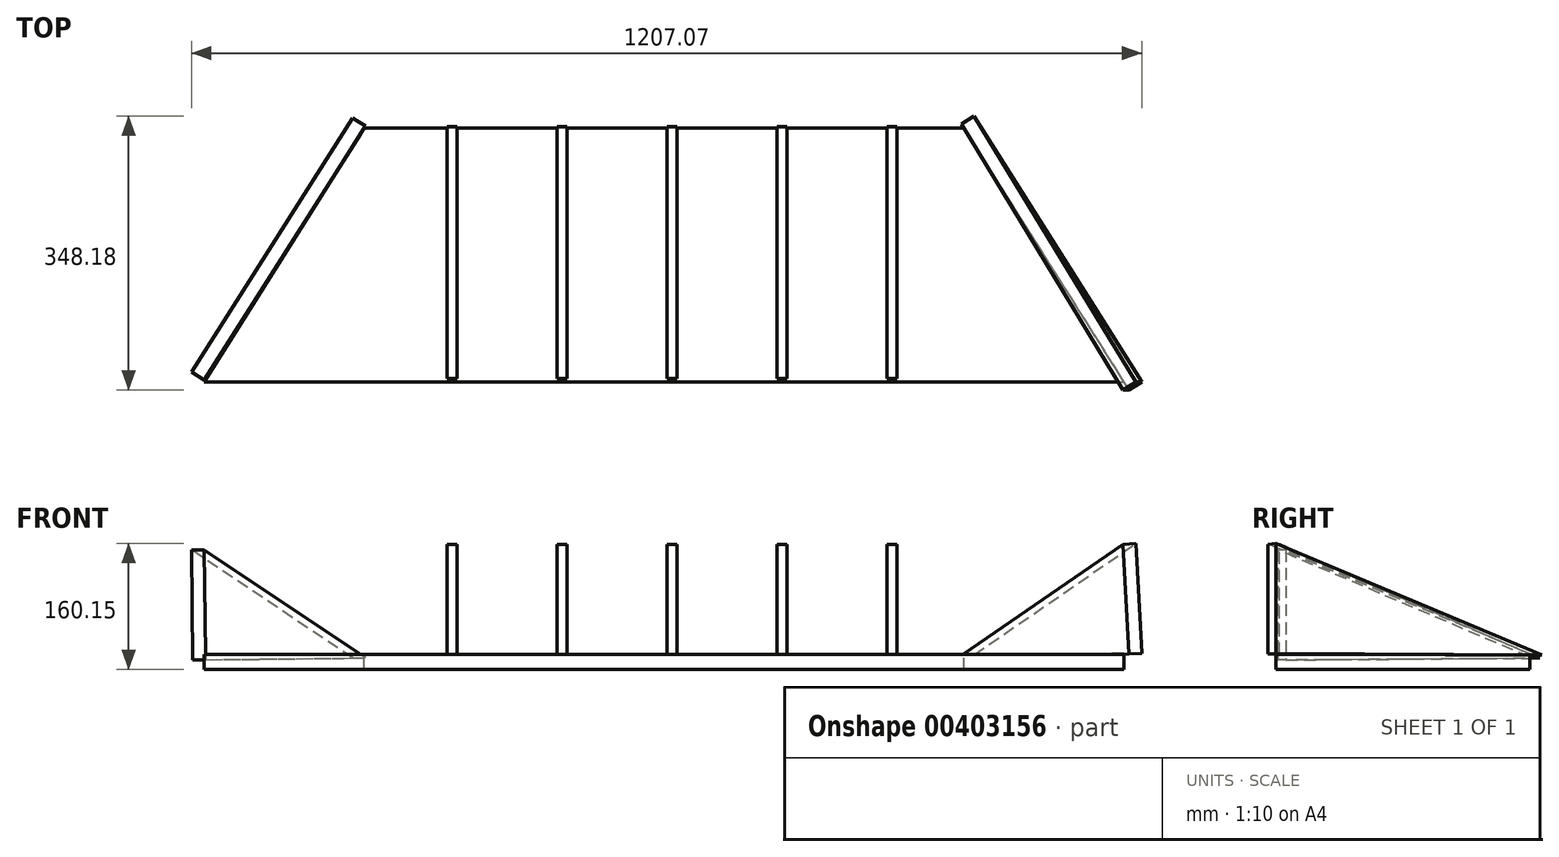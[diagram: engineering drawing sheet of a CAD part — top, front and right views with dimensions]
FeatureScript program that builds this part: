
annotation { "Feature Type Name" : "Feature", "Feature Type Description" : "" }
export const myFeature = defineFeature(function(context is Context, id is Id, definition is map)
    precondition{}
    {
        {
            var Q0;
            Q0=qCreatedBy(makeId("Top.planeOp"),FACE);
            var sketch = newSketch(context, id + "F0", { "sketchPlane" : qUnion([Q0])});
            skLineSegment(sketch, "E0", {"start": v(-587.79, -156.5) * mm, "end": v(580.61, -156.5) * mm});
            skLineSegment(sketch, "E1", {"start": v(580.61, -156.5) * mm, "end": v(377.41, 165.79) * mm});
            skLineSegment(sketch, "E2", {"start": v(377.41, 165.79) * mm, "end": v(-384.59, 165.79) * mm});
            skLineSegment(sketch, "E3", {"start": v(-384.59, 165.79) * mm, "end": v(-587.79, -156.5) * mm});
            skSolve(sketch);
        }
        {
            var Q0;
            Q0=qCreatedBy(makeId("Front.planeOp"),FACE);
            var sketch = newSketch(context, id + "F1", { "sketchPlane" : qUnion([Q0])});
            skLineSegment(sketch, "E4", {"start": v(-588.37, 0) * mm, "end": v(-588.37, 139.7) * mm});
            skLineSegment(sketch, "E5", {"start": v(-588.37, 139.7) * mm, "end": v(580.03, 139.7) * mm});
            skLineSegment(sketch, "E6", {"start": v(580.03, 139.7) * mm, "end": v(580.03, 0) * mm});
            skLineSegment(sketch, "E7", {"start": v(-588.37, 0) * mm, "end": v(580.03, 0) * mm});
            skSolve(sketch);
        }
        {
            var Q0;
            Q0=makeQuery(id+"F1.imprint","IMPRINT",FACE,{"disambiguationData":[TD([[makeQuery(id+"F1.imprint","IMPRINT",EDGE,{"derivedFrom":sQuery(id+"F1.wireOp",EDGE,"E4")}),-1.0]])]});
            extrude(context, id + "F2", {"entities" : qUnion([Q0]), "depth" : 12.7 * mm});
        }
        {
            var Q0;
            Q0=makeQuery(id+"F2.opExtrude","SWEPT_BODY",BODY,{"disambiguationData":[OSD([sQuery(id+"F1.wireOp",EDGE,"E4"),sQuery(id+"F1.wireOp",EDGE,"E5"),sQuery(id+"F1.wireOp",EDGE,"E6"),sQuery(id+"F1.wireOp",EDGE,"E7")])]});
            transform(context, id + "F3", {"entities" : qUnion([Q0]), "transformType" : TransformType.TRANSLATION_3D, "dx" : 0 * mm, "dy" : -154.94 * mm, "dz" : 0 * mm, "makeCopy" : false});
        }
        {
            var Q0;
            Q0=qCreatedBy(makeId("Right.planeOp"),FACE);
            var sketch = newSketch(context, id + "F4", { "sketchPlane" : qUnion([Q0])});
            skLineSegment(sketch, "E8", {"start": v(-152.32, 0) * mm, "end": v(-152.32, 139.7) * mm});
            skLineSegment(sketch, "E9", {"start": v(-152.32, 139.7) * mm, "end": v(167.86, 0) * mm});
            skLineSegment(sketch, "E10", {"start": v(167.86, 0) * mm, "end": v(-152.32, 0) * mm});
            skSolve(sketch);
        }
        {
            var Q0;
            Q0=makeQuery(id+"F4.imprint","IMPRINT",FACE,{"disambiguationData":[TD([[makeQuery(id+"F4.imprint","IMPRINT",EDGE,{"derivedFrom":sQuery(id+"F4.wireOp",EDGE,"E8")}),-1.0]])]});
            extrude(context, id + "F5", {"entities" : qUnion([Q0]), "depth" : 12.7 * mm});
        }
        {
            var Q0;
            Q0=makeQuery(id+"F5.opExtrude","SWEPT_BODY",BODY,{"disambiguationData":[OSD([sQuery(id+"F4.wireOp",EDGE,"E8"),sQuery(id+"F4.wireOp",EDGE,"E9"),sQuery(id+"F4.wireOp",EDGE,"E10")])]});
            var Q1;
            Q1=makeQuery(id+"F5.opExtrude","SWEPT_EDGE",EDGE,{"disambiguationData":[OSD([sQuery(id+"F4.wireOp",EDGE,"E9"),sQuery(id+"F4.wireOp",EDGE,"E10")])]});
            transform(context, id + "F6", {"entities" : qUnion([Q0]), "transformType" : TransformType.TRANSLATION_DISTANCE, "transformDirection" : qUnion([Q1]), "distance" : 139.7 * mm, "makeCopy" : true});
        }
        {
            var Q0;
            Q0=makeQuery(id+"F6.opPattern","COPY",BODY,{"derivedFrom":makeQuery(id+"F5.opExtrude","SWEPT_BODY",BODY,{"disambiguationData":[OSD([sQuery(id+"F4.wireOp",EDGE,"E8"),sQuery(id+"F4.wireOp",EDGE,"E9"),sQuery(id+"F4.wireOp",EDGE,"E10")])]}),"instanceName":"1"});
            var Q1;
            Q1=makeQuery(id+"F6.opPattern","COPY",EDGE,{"derivedFrom":makeQuery(id+"F5.opExtrude","SWEPT_EDGE",EDGE,{"disambiguationData":[OSD([sQuery(id+"F4.wireOp",EDGE,"E9"),sQuery(id+"F4.wireOp",EDGE,"E10")])]}),"instanceName":"1"});
            transform(context, id + "F7", {"entities" : qUnion([Q0]), "transformType" : TransformType.TRANSLATION_DISTANCE, "transformDirection" : qUnion([Q1]), "distance" : 139.7 * mm, "makeCopy" : false});
        }
        {
            var Q0;
            Q0=makeQuery(id+"F5.opExtrude","SWEPT_BODY",BODY,{"disambiguationData":[OSD([sQuery(id+"F4.wireOp",EDGE,"E8"),sQuery(id+"F4.wireOp",EDGE,"E9"),sQuery(id+"F4.wireOp",EDGE,"E10")])]});
            var Q1;
            Q1=makeQuery(id+"F5.opExtrude","SWEPT_EDGE",EDGE,{"disambiguationData":[OSD([sQuery(id+"F4.wireOp",EDGE,"E9"),sQuery(id+"F4.wireOp",EDGE,"E10")])]});
            transform(context, id + "F8", {"entities" : qUnion([Q0]), "transformType" : TransformType.TRANSLATION_DISTANCE, "transformDirection" : qUnion([Q1]), "distance" : 139.7 * mm, "makeCopy" : true});
        }
        {
            var Q0;
            Q0=makeQuery(id+"F6.opPattern","COPY",BODY,{"derivedFrom":makeQuery(id+"F5.opExtrude","SWEPT_BODY",BODY,{"disambiguationData":[OSD([sQuery(id+"F4.wireOp",EDGE,"E8"),sQuery(id+"F4.wireOp",EDGE,"E9"),sQuery(id+"F4.wireOp",EDGE,"E10")])]}),"instanceName":"1"});
            var Q1;
            Q1=makeQuery(id+"F8.opPattern","COPY",BODY,{"derivedFrom":makeQuery(id+"F5.opExtrude","SWEPT_BODY",BODY,{"disambiguationData":[OSD([sQuery(id+"F4.wireOp",EDGE,"E8"),sQuery(id+"F4.wireOp",EDGE,"E9"),sQuery(id+"F4.wireOp",EDGE,"E10")])]}),"instanceName":"1"});
            var Q2;
            Q2=makeQuery(id+"F5.opExtrude","SWEPT_EDGE",EDGE,{"disambiguationData":[OSD([sQuery(id+"F4.wireOp",EDGE,"E9"),sQuery(id+"F4.wireOp",EDGE,"E10")])]});
            transform(context, id + "F9", {"entities" : qUnion([Q0, Q1]), "transformType" : TransformType.TRANSLATION_DISTANCE, "transformDirection" : qUnion([Q2]), "distance" : 419.1 * mm, "oppositeDirection" : true, "makeCopy" : true});
        }
        {
            var Q0;
            Q0=sQuery(id+"F0.wireOp",VERTEX,"E2.start");
            var Q1;
            Q1=sQuery(id+"F0.wireOp",VERTEX,"E1.start");
            var Q2;
            Q2=makeQuery(id+"F2.opExtrude","CAP_VERTEX",VERTEX,{"disambiguationData":[OSD([sQuery(id+"F1.wireOp",EDGE,"E5"),sQuery(id+"F1.wireOp",EDGE,"E6")])],"isStart":false});
            cPlane(context, id + "F10", {"entities" : qUnion([Q0, Q1, Q2]), "cplaneType" : CPlaneType.THREE_POINT, "offset" : 25.4 * mm, "oppositeDirection" : true, "width" : 152.4 * mm, "height" : 152.4 * mm});
        }
        {
            var Q0;
            Q0=qCreatedBy(id+"F10.planeOp",FACE);
            var sketch = newSketch(context, id + "F11", { "sketchPlane" : qUnion([Q0])});
            skLineSegment(sketch, "E11", {"start": v(-54.16, -21.5) * mm, "end": v(-453.6, 108.51) * mm});
            skLineSegment(sketch, "E12", {"start": v(-453.6, 108.51) * mm, "end": v(-453.6, -31.19) * mm});
            skLineSegment(sketch, "E13", {"start": v(-453.6, -31.19) * mm, "end": v(-54.16, -21.5) * mm});
            skSolve(sketch);
        }
        {
            var Q0;
            Q0=makeQuery(id+"F11.imprint","IMPRINT",FACE,{"disambiguationData":[TD([[makeQuery(id+"F11.imprint","IMPRINT",EDGE,{"derivedFrom":sQuery(id+"F11.wireOp",EDGE,"E11")}),1.0]])]});
            extrude(context, id + "F12", {"entities" : qUnion([Q0]), "depth" : 19.05 * mm});
        }
        {
            var Q0;
            Q0=sQuery(id+"F0.wireOp",VERTEX,"E3.start");
            var Q1;
            Q1=makeQuery(id+"F2.opExtrude","CAP_VERTEX",VERTEX,{"disambiguationData":[OSD([sQuery(id+"F1.wireOp",EDGE,"E4"),sQuery(id+"F1.wireOp",EDGE,"E5")])],"isStart":true});
            var Q2;
            Q2=sQuery(id+"F0.wireOp",VERTEX,"E3.end");
            cPlane(context, id + "F13", {"entities" : qUnion([Q0, Q1, Q2]), "cplaneType" : CPlaneType.THREE_POINT, "offset" : 25.4 * mm, "width" : 152.4 * mm, "height" : 152.4 * mm});
        }
        {
            var Q0;
            Q0=qCreatedBy(id+"F13.planeOp",FACE);
            var sketch = newSketch(context, id + "F14", { "sketchPlane" : qUnion([Q0])});
            skLineSegment(sketch, "E14", {"start": v(61.93, 0) * mm, "end": v(442.93, 139.7) * mm});
            skLineSegment(sketch, "E15", {"start": v(442.93, 139.7) * mm, "end": v(442.93, 0) * mm});
            skLineSegment(sketch, "E16", {"start": v(442.93, 0) * mm, "end": v(61.93, 0) * mm});
            skSolve(sketch);
        }
        {
            var Q0;
            Q0 = qSketchRegion(id + "F14", true);
            extrude(context, id + "F15", {"entities" : qUnion([Q0]), "depth" : 19.05 * mm});
        }
        {
            var Q0;
            Q0=makeQuery(id+"F2.opExtrude","SWEPT_BODY",BODY,{"disambiguationData":[OSD([sQuery(id+"F1.wireOp",EDGE,"E4"),sQuery(id+"F1.wireOp",EDGE,"E5"),sQuery(id+"F1.wireOp",EDGE,"E6"),sQuery(id+"F1.wireOp",EDGE,"E7")])]});
            deleteBodies(context, id + "F16", {"entities" : qUnion([Q0])});
        }
        {
            var Q0;
            Q0 = qSketchRegion(id + "F0", true);
            extrude(context, id + "F17", {"entities" : qUnion([Q0]), "oppositeDirection" : true, "depth" : 19.05 * mm});
        }
    });
